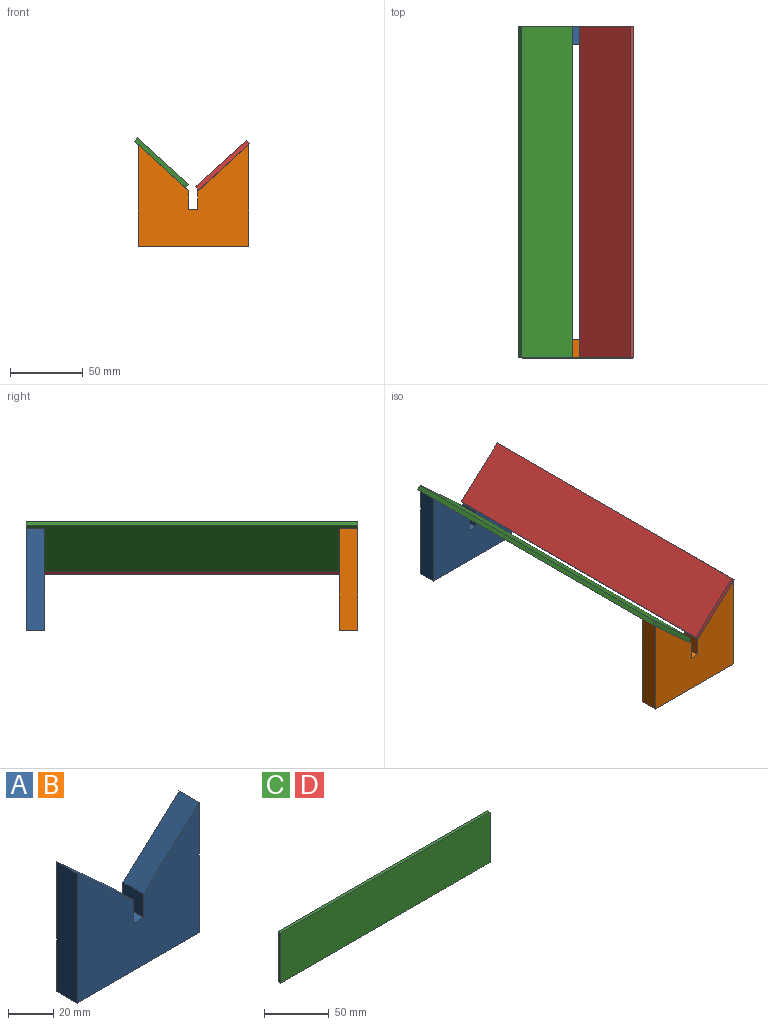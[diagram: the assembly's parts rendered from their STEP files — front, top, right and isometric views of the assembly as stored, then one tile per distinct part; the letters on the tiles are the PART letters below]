
ASSEMBLY  parts=4 mates=8
PART A: 10 faces, bbox 76.2x12.7x69.9 mm
  f0: plane 69.85x12.7mm, normal (-1,0,0), area 887.1mm2, adj f1,f7,f8,f9
  f1: plane 76.2x12.7mm, normal (0,0,-1), area 967.7mm2, adj f0,f2,f8,f9
  f2: plane 69.85x12.7mm, normal (1,0,0), area 887.1mm2, adj f1,f3,f8,f9
  f3: plane 34.93x31.75mm, normal (-0.67,0,0.74), area 599.4mm2, adj f2,f4,f8,f9
  f4: plane 12.7x12.7mm, normal (-1,0,0), area 161.3mm2, adj f3,f5,f8,f9
  f5: plane 12.7x6.35mm, normal (0,0,1), area 80.6mm2, adj f4,f6,f8,f9
  f6: plane 12.7x12.7mm, normal (1,0,0), area 161.3mm2, adj f5,f7,f8,f9
  f7: plane 34.93x31.75mm, normal (0.67,0,0.74), area 599.4mm2, adj f0,f6,f8,f9
  f8: plane 76.2x69.85mm, normal (0,-1,0), area 3931.4mm2, adj f0,f1,f2,f3,f4,f5,f6,f7
  f9: plane 76.2x69.85mm, normal (0,1,0), area 3931.4mm2, adj f0,f1,f2,f3,f4,f5,f6,f7
PART B: same geometry as A
PART C: 6 faces, bbox 228.6x3.2x47.6 mm
  f0: plane 47.63x3.18mm, normal (1,0,0), area 151.2mm2, adj f1,f3,f4,f5
  f1: plane 228.6x3.18mm, normal (0,0,1), area 725.8mm2, adj f0,f2,f4,f5
  f2: plane 47.63x3.18mm, normal (-1,0,0), area 151.2mm2, adj f1,f3,f4,f5
  f3: plane 228.6x3.18mm, normal (0,0,-1), area 725.8mm2, adj f0,f2,f4,f5
  f4: plane 228.6x47.63mm, normal (0,-1,0), area 10887.1mm2, adj f0,f1,f2,f3
  f5: plane 228.6x47.63mm, normal (0,1,0), area 10887.1mm2, adj f0,f1,f2,f3
PART D: same geometry as C
PLACE A t=(-76.57,215.9,0)mm
PLACE B t=(-76.57,0,0)mm fixed
PLACE C rot(axis=(-0.38,-0.38,0.85),99.4deg) t=(-86.8,-25.5,33.1)mm
PLACE D rot(axis=(0.38,0.38,0.85),99.4deg) t=(-95.48,-25.5,33.73)mm
MATE planar B.f3 <-> D.f4  axis (-0.67,0,0.74) through (-68.49,-6.35,53.97)mm
MATE planar D.f2 <-> B.f8  axis (0,-1,0) through (-68.97,-12.7,55.68)mm
MATE planar B.f7 <-> C.f5  axis (0.67,0,0.74) through (-109.76,-6.35,53.98)mm
MATE planar A.f0 <-> B.f0  axis (-1,0,0) through (-127.22,209.55,34.93)mm
MATE planar C.f2 <-> B.f8  axis (0,-1,0) through (-111.17,-12.7,57.4)mm
MATE parallel A.f9 <-> D.f0  axis (0,1,0) through (-85.95,215.9,25.4)mm
MATE planar A.f1 <-> B.f1  axis (0,0,-1) through (-89.12,209.55,0)mm
MATE planar A.f9 <-> D.f0  axis (0,1,0) through (-89.12,215.9,27.15)mm
